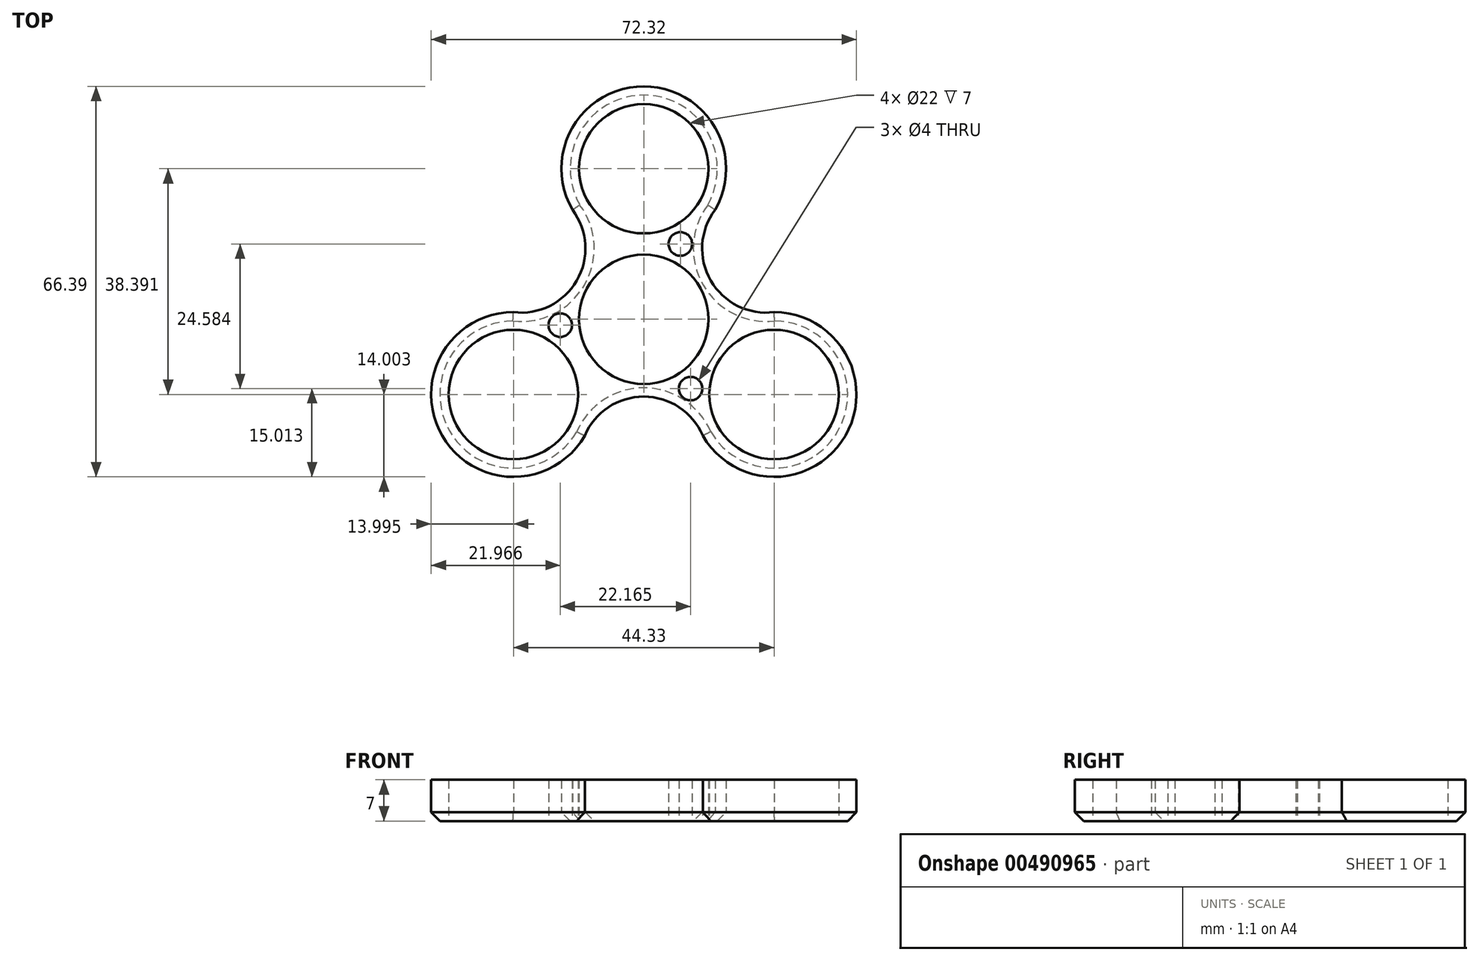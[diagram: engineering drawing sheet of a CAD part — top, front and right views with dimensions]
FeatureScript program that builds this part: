
annotation { "Feature Type Name" : "Feature", "Feature Type Description" : "" }
export const myFeature = defineFeature(function(context is Context, id is Id, definition is map)
    precondition{}
    {
        {
            var Q0;
            Q0=qCreatedBy(makeId("Top.planeOp"),FACE);
            var sketch = newSketch(context, id + "F0", { "sketchPlane" : qUnion([Q0])});
            skCircle(sketch, "E0", {"center": v(0, 0) * mm, "radius": 11 * mm});
            skCircle(sketch, "E1", {"center": v(0, 25.6) * mm, "radius": 11 * mm});
            skArc(sketch, "E2.0", {"start": v(12.12, 18.6) * mm, "mid": v(0, 39.6) * mm, "end": v(-12.12, 18.6) * mm});
            skLineSegment(sketch, "E3", {"start": v(0, 25.6) * mm, "end": v(-9.53, 20.1) * mm});
            skLineSegment(sketch, "E4.MirrorCS", {"start": v(0, 25.6) * mm, "end": v(9.53, 20.1) * mm});
            skArc(sketch, "E5.1.0", {"start": v(-22.16, 1.2) * mm, "mid": v(-34.29, -19.8) * mm, "end": v(-10.04, -19.8) * mm});
            skCircle(sketch, "E5.1.1", {"center": v(-22.16, -12.8) * mm, "radius": 11 * mm});
            skArc(sketch, "E5.2.0", {"start": v(10.04, -19.8) * mm, "mid": v(34.29, -19.8) * mm, "end": v(22.16, 1.2) * mm});
            skCircle(sketch, "E5.2.1", {"center": v(22.16, -12.8) * mm, "radius": 11 * mm});
            skArc(sketch, "E6", {"start": v(-22.16, 1.2) * mm, "mid": v(-11.4, 6.58) * mm, "end": v(-12.12, 18.6) * mm});
            skArc(sketch, "E7.1.0", {"start": v(10.04, -19.8) * mm, "mid": v(0, -13.15) * mm, "end": v(-10.04, -19.8) * mm});
            skArc(sketch, "E7.2.0", {"start": v(12.12, 18.6) * mm, "mid": v(11.4, 6.58) * mm, "end": v(22.16, 1.2) * mm});
            skLineSegment(sketch, "E8", {"start": v(0, 11) * mm, "end": v(0, 14.6) * mm});
            skLineSegment(sketch, "E9", {"start": v(-4.98, 12.8) * mm, "end": v(-7.47, 12.8) * mm});
            skPoint(sketch, "E10", {"position": v(-4.98, 12.8) * mm});
            skPoint(sketch, "E11.orphan", {"position": v(0, 12.8) * mm});
            skPoint(sketch, "E12", {"position": v(-7.47, 12.8) * mm});
            skPoint(sketch, "E13.orphan", {"position": v(-9.96, 12.8) * mm});
            skPoint(sketch, "E14", {"position": v(-6.22, 12.8) * mm});
            skCircle(sketch, "E15", {"center": v(-6.22, 12.8) * mm, "radius": 2 * mm});
            skCircle(sketch, "E16.MirrorC", {"center": v(6.22, 12.8) * mm, "radius": 2 * mm});
            skCircle(sketch, "E17.1.0", {"center": v(-7.97, -11.79) * mm, "radius": 2 * mm});
            skCircle(sketch, "E17.1.1", {"center": v(-14.2, -1) * mm, "radius": 2 * mm});
            skCircle(sketch, "E17.2.0", {"center": v(14.2, -1) * mm, "radius": 2 * mm});
            skCircle(sketch, "E17.2.1", {"center": v(7.97, -11.79) * mm, "radius": 2 * mm});
            skSolve(sketch);
        }
        {
            var Q0;
            Q0=makeQuery(id+"F0.imprint","IMPRINT",FACE,{"disambiguationData":[TD([[makeQuery(id+"F0.imprint","IMPRINT",EDGE,{"derivedFrom":sQuery(id+"F0.wireOp",EDGE,"E0")}),-1.0]])]});
            extrude(context, id + "F1", {"entities" : qUnion([Q0]), "depth" : 3.5 * mm});
        }
        {
            var Q0;
            Q0=makeQuery(id+"F0.imprint","IMPRINT",FACE,{"disambiguationData":[TD([[makeQuery(id+"F0.imprint","IMPRINT",EDGE,{"derivedFrom":sQuery(id+"F0.wireOp",EDGE,"E15")}),1.0]])]});
            var Q1;
            Q1=makeQuery(id+"F0.imprint","IMPRINT",FACE,{"disambiguationData":[TD([[makeQuery(id+"F0.imprint","IMPRINT",EDGE,{"derivedFrom":sQuery(id+"F0.wireOp",EDGE,"E16.MirrorC")}),-1.0]])]});
            var Q2;
            Q2=makeQuery(id+"F0.imprint","IMPRINT",FACE,{"disambiguationData":[TD([[makeQuery(id+"F0.imprint","IMPRINT",EDGE,{"derivedFrom":sQuery(id+"F0.wireOp",EDGE,"E17.2.0")}),1.0]])]});
            var Q3;
            Q3=makeQuery(id+"F0.imprint","IMPRINT",FACE,{"disambiguationData":[TD([[makeQuery(id+"F0.imprint","IMPRINT",EDGE,{"derivedFrom":sQuery(id+"F0.wireOp",EDGE,"E17.2.1")}),-1.0]])]});
            var Q4;
            Q4=makeQuery(id+"F0.imprint","IMPRINT",FACE,{"disambiguationData":[TD([[makeQuery(id+"F0.imprint","IMPRINT",EDGE,{"derivedFrom":sQuery(id+"F0.wireOp",EDGE,"E17.1.0")}),1.0]])]});
            var Q5;
            Q5=makeQuery(id+"F0.imprint","IMPRINT",FACE,{"disambiguationData":[TD([[makeQuery(id+"F0.imprint","IMPRINT",EDGE,{"derivedFrom":sQuery(id+"F0.wireOp",EDGE,"E17.1.1")}),-1.0]])]});
            extrude(context, id + "F2", {"entities" : qUnion([Q0, Q1, Q2, Q3, Q4, Q5]), "operationType" : NewBodyOperationType.ADD, "depth" : 7 * mm});
        }
        {
            var Q0;
            Q0=makeQuery(id+"F1.opExtrude","CAP_EDGE",EDGE,{"disambiguationData":[OSD([sQuery(id+"F0.wireOp",EDGE,"E2.0")])],"isStart":true});
            var Q1;
            Q1=makeQuery(id+"F1.opExtrude","CAP_EDGE",EDGE,{"disambiguationData":[OSD([sQuery(id+"F0.wireOp",EDGE,"E6")])],"isStart":true});
            var Q2;
            Q2=makeQuery(id+"F1.opExtrude","CAP_EDGE",EDGE,{"disambiguationData":[OSD([sQuery(id+"F0.wireOp",EDGE,"E5.1.0")])],"isStart":true});
            var Q3;
            Q3=makeQuery(id+"F1.opExtrude","CAP_EDGE",EDGE,{"disambiguationData":[OSD([sQuery(id+"F0.wireOp",EDGE,"E7.1.0")])],"isStart":true});
            var Q4;
            Q4=makeQuery(id+"F1.opExtrude","CAP_EDGE",EDGE,{"disambiguationData":[OSD([sQuery(id+"F0.wireOp",EDGE,"E5.2.0")])],"isStart":true});
            var Q5;
            Q5=makeQuery(id+"F1.opExtrude","CAP_EDGE",EDGE,{"disambiguationData":[OSD([sQuery(id+"F0.wireOp",EDGE,"E7.2.0")])],"isStart":true});
            chamfer(context, id + "F3", {"entities" : qUnion([Q0, Q1, Q2, Q3, Q4, Q5]), "width" : 1.5 * mm, "tangentPropagation" : true});
        }
    });
